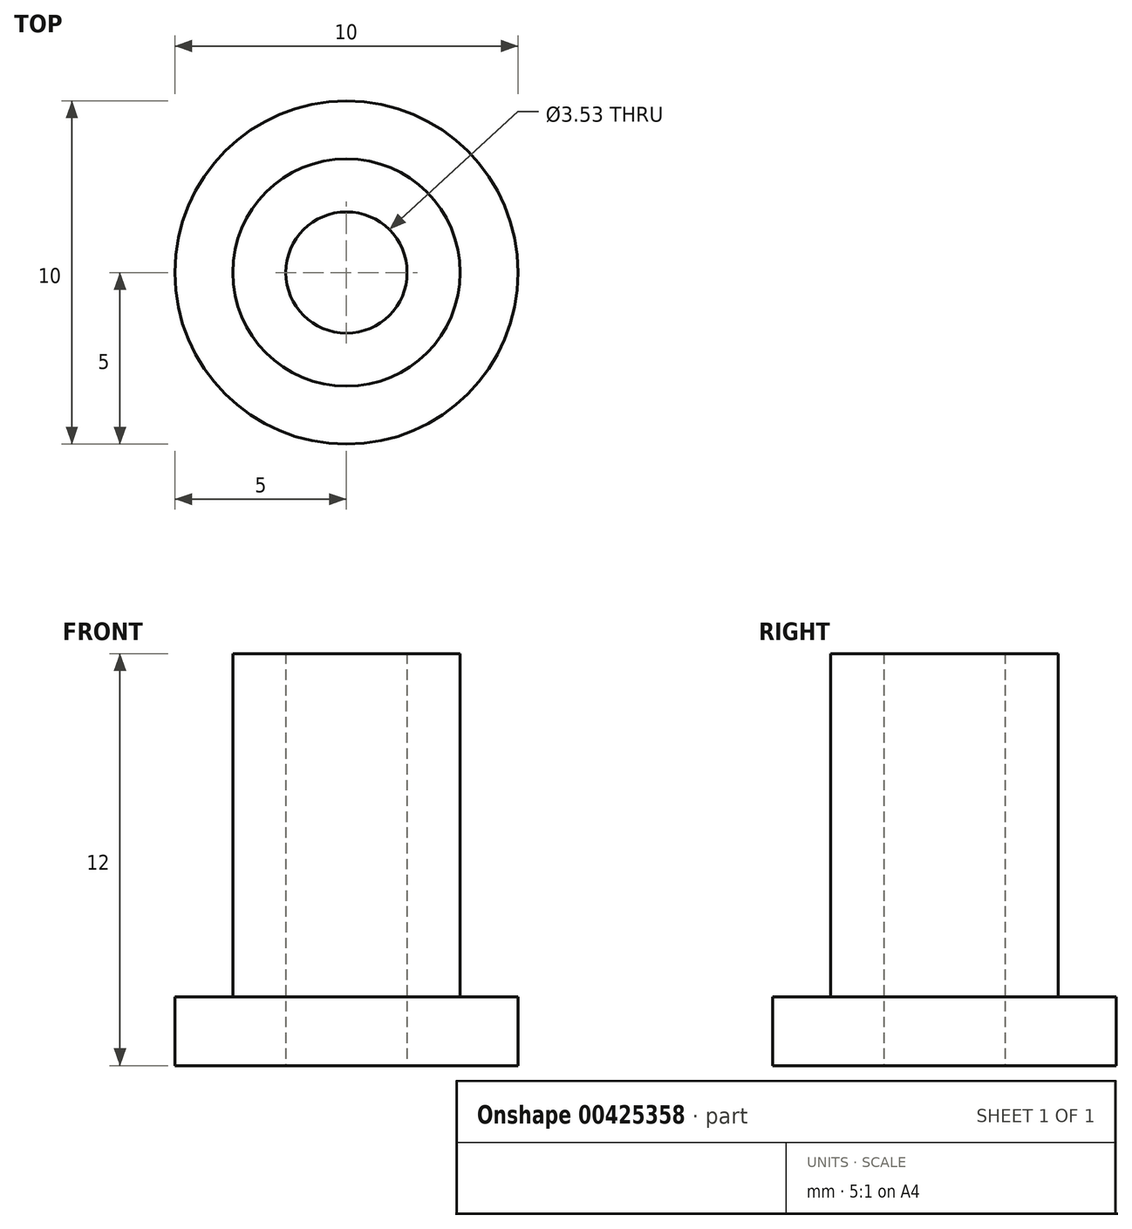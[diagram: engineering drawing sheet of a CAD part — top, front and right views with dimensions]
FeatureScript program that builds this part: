
annotation { "Feature Type Name" : "Feature", "Feature Type Description" : "" }
export const myFeature = defineFeature(function(context is Context, id is Id, definition is map)
    precondition{}
    {
        {
            var Q0;
            Q0=qCreatedBy(makeId("Top.planeOp"),FACE);
            var sketch = newSketch(context, id + "F0", { "sketchPlane" : qUnion([Q0])});
            skCircle(sketch, "E0", {"center": v(0, 0) * mm, "radius": 1.77 * mm});
            skCircle(sketch, "E1", {"center": v(0, 0) * mm, "radius": 3.31 * mm});
            skSolve(sketch);
        }
        {
            var Q0;
            Q0=makeQuery(id+"F0.imprint","IMPRINT",FACE,{"disambiguationData":[TD([[makeQuery(id+"F0.imprint","IMPRINT",EDGE,{"derivedFrom":sQuery(id+"F0.wireOp",EDGE,"E0")}),-1.0]])]});
            extrude(context, id + "F1", {"entities" : qUnion([Q0]), "depth" : 10 * mm});
        }
        {
            var Q0;
            Q0=makeQuery(id+"F1.opExtrude","CAP_FACE",FACE,{"disambiguationData":[OSD([sQuery(id+"F0.wireOp",EDGE,"E0"),sQuery(id+"F0.wireOp",EDGE,"E1")])],"isStart":true});
            var sketch = newSketch(context, id + "F2", { "sketchPlane" : qUnion([Q0])});
            skCircle(sketch, "E2", {"center": v(0, 0) * mm, "radius": 1.77 * mm});
            skCircle(sketch, "E3", {"center": v(0, 0) * mm, "radius": 5 * mm});
            skSolve(sketch);
        }
        {
            var Q0;
            Q0=qSketchRegion(id+"F2",true);
            extrude(context, id + "F3", {"entities" : qUnion([Q0]), "operationType" : NewBodyOperationType.ADD, "depth" : 2 * mm});
        }
    });
